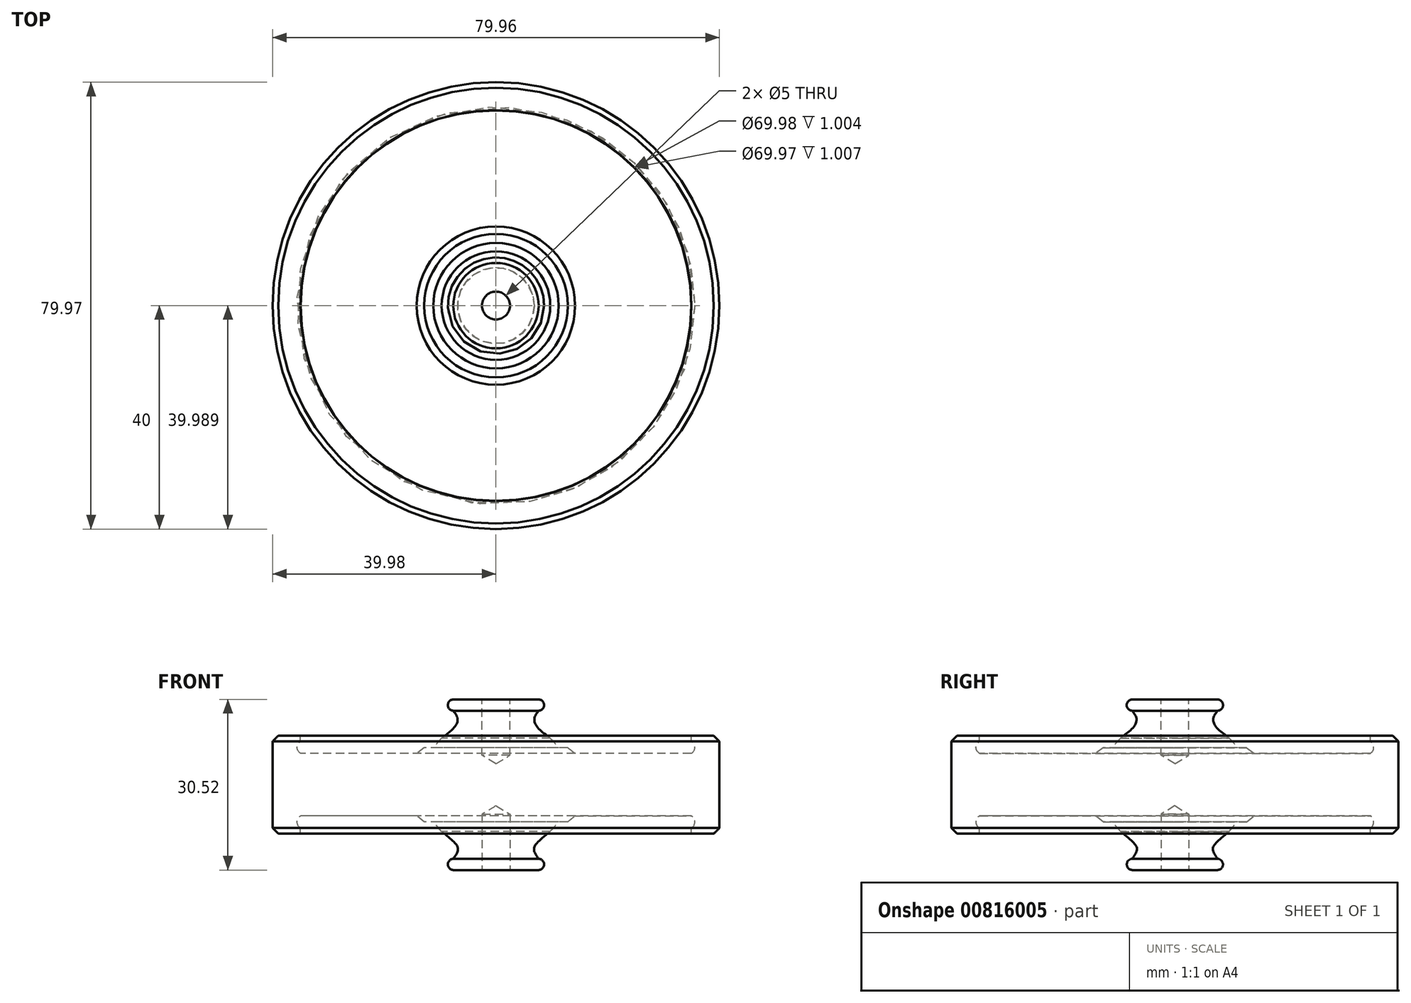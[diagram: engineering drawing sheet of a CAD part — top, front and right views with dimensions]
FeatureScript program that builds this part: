
annotation { "Feature Type Name" : "Feature", "Feature Type Description" : "" }
export const myFeature = defineFeature(function(context is Context, id is Id, definition is map)
    precondition{}
    {
        {
            var Q0;
            Q0=qCreatedBy(makeId("Right.planeOp"),FACE);
            var sketch = newSketch(context, id + "F0", { "sketchPlane" : qUnion([Q0])});
            skPoint(sketch, "E0", {"position": v(-7.66, 15.25) * mm});
            skPoint(sketch, "E1", {"position": v(-9.73, -8.36) * mm});
            skLineSegment(sketch, "E2", {"start": v(-35, -7.76) * mm, "end": v(-35, -8.77) * mm});
            skLineSegment(sketch, "E3", {"start": v(-35, -8.77) * mm, "end": v(-40, -8.77) * mm});
            skLineSegment(sketch, "E4", {"start": v(-40, 8.75) * mm, "end": v(-35, 8.75) * mm});
            skLineSegment(sketch, "E5", {"start": v(-35, 8.75) * mm, "end": v(-35, 7.75) * mm});
            skLineSegment(sketch, "E6", {"start": v(-23.01, 5.57) * mm, "end": v(-34.95, 5.57) * mm});
            skArc(sketch, "E7", {"start": v(-35, 7.75) * mm, "mid": v(-35.6, 6.65) * mm, "end": v(-34.95, 5.57) * mm});
            skArc(sketch, "E8", {"start": v(-34.97, -5.58) * mm, "mid": v(-35.59, -6.67) * mm, "end": v(-35, -7.76) * mm});
            skFitSpline(sketch, "E9", {"points": [v(-9.73, -8.36) * mm, v(-7.2, -10.62) * mm, v(-6.82, -11.37) * mm, v(-6.93, -12.06) * mm, v(-7.64, -13.26) * mm], "startDerivative": vector(7.97, -6.52) * mm, "endDerivative": vector(-3.46, -5.08) * mm});
            skArc(sketch, "E10", {"start": v(-7.64, -13.26) * mm, "mid": v(-8.62, -14.25) * mm, "end": v(-7.66, -15.27) * mm});
            skArc(sketch, "E11", {"start": v(-7.66, 15.25) * mm, "mid": v(-8.63, 14.25) * mm, "end": v(-7.66, 13.25) * mm});
            skLineSegment(sketch, "E12", {"start": v(-23.01, 5.57) * mm, "end": v(-14.18, 5.57) * mm});
            skLineSegment(sketch, "E13", {"start": v(-14.18, 5.57) * mm, "end": v(-12.85, 6.64) * mm});
            skLineSegment(sketch, "E14", {"start": v(-12.85, 6.64) * mm, "end": v(-11.23, 6.64) * mm});
            skLineSegment(sketch, "E15", {"start": v(-11.23, 6.64) * mm, "end": v(-9.73, 8.36) * mm});
            skLineSegment(sketch, "E16.MirrorCS", {"start": v(-12.85, -6.64) * mm, "end": v(-11.23, -6.64) * mm});
            skLineSegment(sketch, "E17.MirrorCS", {"start": v(-14.18, -5.58) * mm, "end": v(-12.85, -6.64) * mm});
            skLineSegment(sketch, "E18", {"start": v(-40, 8.75) * mm, "end": v(-40, -8.77) * mm});
            skLineSegment(sketch, "E19", {"start": v(-0.01, 15.25) * mm, "end": v(-0.01, -15.27) * mm});
            skLineSegment(sketch, "E20", {"start": v(-7.66, 15.25) * mm, "end": v(-0.01, 15.25) * mm});
            skLineSegment(sketch, "E21", {"start": v(-7.66, -15.27) * mm, "end": v(-0.01, -15.27) * mm});
            skLineSegment(sketch, "E22", {"start": v(-14.18, -5.58) * mm, "end": v(-34.97, -5.58) * mm});
            skPoint(sketch, "E23", {"position": v(-6.94, 12.05) * mm});
            skPoint(sketch, "E24", {"position": v(-7.2, 10.6) * mm});
            skPoint(sketch, "E25", {"position": v(-9.73, 8.36) * mm});
            skFitSpline(sketch, "E26", {"points": [v(-9.73, 8.36) * mm, v(-7.2, 10.6) * mm, v(-6.94, 12.05) * mm, v(-7.66, 13.25) * mm], "startDerivative": vector(7.06, 5.16) * mm, "endDerivative": vector(-3.25, 4.1) * mm});
            skLineSegment(sketch, "E27", {"start": v(-9.73, -8.36) * mm, "end": v(-11.23, -6.64) * mm});
            skSolve(sketch);
        }
        {
            var Q0;
            Q0 = qSketchRegion(id + "F0", true);
            var Q1;
            Q1=sQuery(id+"F0.wireOp",EDGE,"E19");
            revolve(context, id + "F1", {"surfaceOperationType" : NewSurfaceOperationType.NEW, "entities" : qUnion([Q0]), "axis" : qUnion([Q1]), "revolveType" : RevolveType.FULL});
        }
        {
            var Q0;
            Q0=makeQuery(id+"F1.opRevolve","SWEPT_EDGE",EDGE,{"disambiguationData":[OSD([sQuery(id+"F0.wireOp",EDGE,"E4"),sQuery(id+"F0.wireOp",EDGE,"E18")])]});
            var Q1;
            Q1=makeQuery(id+"F1.opRevolve","SWEPT_EDGE",EDGE,{"disambiguationData":[OSD([sQuery(id+"F0.wireOp",EDGE,"E3"),sQuery(id+"F0.wireOp",EDGE,"E18")])]});
            chamfer(context, id + "F2", {"entities" : qUnion([Q0, Q1]), "width" : 1 * mm, "tangentPropagation" : true});
        }
        {
            var Q0;
            Q0=makeQuery(id+"F1.opRevolve","SWEPT_FACE",FACE,{"disambiguationData":[OSD([sQuery(id+"F0.wireOp",EDGE,"E20")])]});
            var sketch = newSketch(context, id + "F3", { "sketchPlane" : qUnion([Q0])});
            skCircle(sketch, "E28", {"center": v(0, 0) * mm, "radius": 2.5 * mm});
            skSolve(sketch);
        }
        {
            var Q0;
            Q0=sQuery(id+"F3.wireOp",VERTEX,"E28.center");
            var Q1;
            Q1=makeQuery(id+"F1.opRevolve","SWEPT_BODY",BODY,{"disambiguationData":[OSD([sQuery(id+"F0.wireOp",EDGE,"E2"),sQuery(id+"F0.wireOp",EDGE,"E3"),sQuery(id+"F0.wireOp",EDGE,"E4"),sQuery(id+"F0.wireOp",EDGE,"E5"),sQuery(id+"F0.wireOp",EDGE,"E6"),sQuery(id+"F0.wireOp",EDGE,"E7"),sQuery(id+"F0.wireOp",EDGE,"E8"),sQuery(id+"F0.wireOp",EDGE,"E9"),sQuery(id+"F0.wireOp",EDGE,"E10"),sQuery(id+"F0.wireOp",EDGE,"E11"),sQuery(id+"F0.wireOp",EDGE,"E12"),sQuery(id+"F0.wireOp",EDGE,"E13"),sQuery(id+"F0.wireOp",EDGE,"E14"),sQuery(id+"F0.wireOp",EDGE,"E15"),sQuery(id+"F0.wireOp",EDGE,"E16.MirrorCS"),sQuery(id+"F0.wireOp",EDGE,"E17.MirrorCS"),sQuery(id+"F0.wireOp",EDGE,"E18"),sQuery(id+"F0.wireOp",EDGE,"E19"),sQuery(id+"F0.wireOp",EDGE,"E20"),sQuery(id+"F0.wireOp",EDGE,"E21"),sQuery(id+"F0.wireOp",EDGE,"E22"),sQuery(id+"F0.wireOp",EDGE,"E26"),sQuery(id+"F0.wireOp",EDGE,"E27")])]});
            hole(context, id + "F4", {"style" : HoleStyle.SIMPLE, "endStyle" : HoleEndStyle.BLIND, "standardTappedOrClearance" : lookupTablePath({ "standard" : "ISO", "engagement" : "75%", "pitch" : "1 mm", "size" : "M6", "type" : "Tapped" }), "standardBlindInLast" : lookupTablePath({ "standard" : "ISO", "engagement" : "75%", "pitch" : "1 mm", "size" : "M6", "type" : "Tapped" }), "holeDiameter" : 5 * mm, "majorDiameter" : 6 * mm, "showTappedDepth" : true, "holeDepth" : 10 * mm, "isTappedThrough" : true, "tappedDepth" : 7 * mm, "tapClearance" : 3, "locations" : qUnion([Q0]), "scope" : qUnion([Q1])});
        }
        {
            var Q0;
            Q0=makeQuery(id+"F1.opRevolve","SWEPT_FACE",FACE,{"disambiguationData":[OSD([sQuery(id+"F0.wireOp",EDGE,"E21")])]});
            var sketch = newSketch(context, id + "F5", { "sketchPlane" : qUnion([Q0])});
            skCircle(sketch, "E29", {"center": v(0, 0) * mm, "radius": 2.5 * mm});
            skSolve(sketch);
        }
        {
            var Q0;
            Q0=sQuery(id+"F5.wireOp",VERTEX,"E29.center");
            var Q1;
            Q1=makeQuery(id+"F1.opRevolve","SWEPT_BODY",BODY,{"disambiguationData":[OSD([sQuery(id+"F0.wireOp",EDGE,"E2"),sQuery(id+"F0.wireOp",EDGE,"E3"),sQuery(id+"F0.wireOp",EDGE,"E4"),sQuery(id+"F0.wireOp",EDGE,"E5"),sQuery(id+"F0.wireOp",EDGE,"E6"),sQuery(id+"F0.wireOp",EDGE,"E7"),sQuery(id+"F0.wireOp",EDGE,"E8"),sQuery(id+"F0.wireOp",EDGE,"E9"),sQuery(id+"F0.wireOp",EDGE,"E10"),sQuery(id+"F0.wireOp",EDGE,"E11"),sQuery(id+"F0.wireOp",EDGE,"E12"),sQuery(id+"F0.wireOp",EDGE,"E13"),sQuery(id+"F0.wireOp",EDGE,"E14"),sQuery(id+"F0.wireOp",EDGE,"E15"),sQuery(id+"F0.wireOp",EDGE,"E16.MirrorCS"),sQuery(id+"F0.wireOp",EDGE,"E17.MirrorCS"),sQuery(id+"F0.wireOp",EDGE,"E18"),sQuery(id+"F0.wireOp",EDGE,"E19"),sQuery(id+"F0.wireOp",EDGE,"E20"),sQuery(id+"F0.wireOp",EDGE,"E21"),sQuery(id+"F0.wireOp",EDGE,"E22"),sQuery(id+"F0.wireOp",EDGE,"E26"),sQuery(id+"F0.wireOp",EDGE,"E27")])]});
            hole(context, id + "F6", {"style" : HoleStyle.SIMPLE, "endStyle" : HoleEndStyle.BLIND, "standardTappedOrClearance" : lookupTablePath({ "standard" : "ISO", "engagement" : "75%", "pitch" : "1 mm", "size" : "M6", "type" : "Tapped" }), "standardBlindInLast" : lookupTablePath({ "standard" : "ISO", "engagement" : "75%", "pitch" : "1 mm", "size" : "M6", "type" : "Tapped" }), "holeDiameter" : 5 * mm, "majorDiameter" : 6 * mm, "showTappedDepth" : true, "holeDepth" : 10 * mm, "isTappedThrough" : true, "tappedDepth" : 7 * mm, "tapClearance" : 3, "locations" : qUnion([Q0]), "scope" : qUnion([Q1])});
        }
    });
